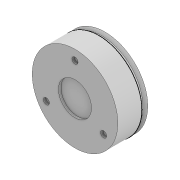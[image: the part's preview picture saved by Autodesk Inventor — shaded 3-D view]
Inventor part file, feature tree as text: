
AUTODESK INVENTOR PART (.ipt)
format: ipt  version: 2020 (Build 240168000, 168)  size: 129,536 bytes
history: native  units: mm
features: sketch x6, other x5, extrude x3, loft x2, projected_geometry x1
ambient origin geometry x8: Origin, YZ Plane, XZ Plane, XY Plane, X Axis, Y Axis, Z Axis, Center Point
bodies: Body1 (feature_tree)
feature tree (17):
  other  "솔리드1"
  extrude  "돌출1"  Depth=70.0mm
  extrude  "돌출2"  Depth=19.5mm TaperAngle=0.0deg
  sketch  "스케치3"
  other  "작업 평면1"
  loft  "로프트1"
  other  "작업 평면2"
  loft  "로프트2"
  extrude  "돌출3"  Depth=30.0mm TaperAngle=360.0deg
  sketch  "스케치1"
  sketch  "스케치2"
  projected_geometry  "투영된 루프1"
  sketch  "스케치4"
  other  "모서리1"
  sketch  "스케치5"
  other  "모서리2"
  sketch  "스케치6"
